# Revit family: Luminaria REALIA
name_source: partatom
category: Luminarias
revit_build: Autodesk Revit 2016 (Build: 20150220_1215(x64)
units: mm (PartAtom-declared; Revit-internal decimal feet)

## family parameters
Compartido = No
Corte con vacíos al cargar = No
Cota de conector redondo = Diámetro de uso
Número OmniClass = 23.80.70.00
Origen de luz = Sí
Punto de cálculo de habitación = No
Se basa en plano de trabajo = No
Siempre vertical = No
Tipo de pieza = Normal
Título OmniClass = Lighting

## types (1)
- REALIA 32 LED 700mA 71W 4000K T4
    Ajuste de potencia = Si
    Alto = 700 mm
    Altura columna = 3-6 m
    Ancho = 435 mm
    Anchura rectángulo de emisión = 227 mm  [stored 0.744751 ft]
    Archivo de red fotométrica = ILRE03244_REALIA32LED700mA71W4000KT4-10785.ies
    Cambio de temperatura de color de luz atenuada = <Ninguno>
    Carga aparente = 0 VA
    Certificaciones = CE, ENEC, AENOR, CB SCHEME, RETILAP.
    Clase de aislamiento = Clase I / Clase II
    Classificación = Iluminación
    Comentarios de tipo = Luminaria clásica con un diseño modernista. Incorpora todos los detalles técnicos
necesarios para vestir espacios históricos y entornos urbanos.
    Comentarios de vataje = 1
    Descripción = Disponible en LEDs y para lámparas de descarga con reflector anodizado y también
con reflector eXtreme con 15 posiciones.Cuerpo en inyección de aluminio de alta resistencia.Apertura manual mediante bellota roscada sin necesidad de herramientas.Portalámparas regulable en sentido longitudinal de la lámpara.Posibilidad de difusores laterales bajo demanda.Color negro micro texturado.
    Diametro fijación = Top 60 mm o 3/4" GAS
    Difusor = Cristal
    Driver = Incluido
    Fabricante = BENITO
    Ficha tecnica = http://www.benito.com
    Filtro de color = 16777215
    Forma visible en renderización = No
    Frequencia nominal = 50/60 Hz
    Indice de reproducción cromatica = >70
    Instrucciones de montaje = http://www.benito.com
    Longitud de rectángulo de emisión = 172 mm  [stored 0.564304 ft]
    Lámpara = Led
    Material cuerpo = Aluminio
    Modelo = REALIA 32 LED 700 mA 71W 4000K
    Peso = 7,9 Kg
    Protección IP = 66
    Protección impacto IK = 09
    Referencia = ILVI75MI2
    Regulable = Si
    Sistema regulable = SI
    Tipo de opticas = T2,T4
    URL = http://www.benito.com
    URL producto = http://www.benito.com
    Voltage nominal = 220-240 V AC
    Ángulo de inclinación = 90.00°

note: [stored X ft] marks values corroborated as IEEE doubles in the binary element streams (Revit-internal decimal feet)

## geometry (parser evidence)
native form markers: Blend x4
no freeform markers — native parametric forms only
